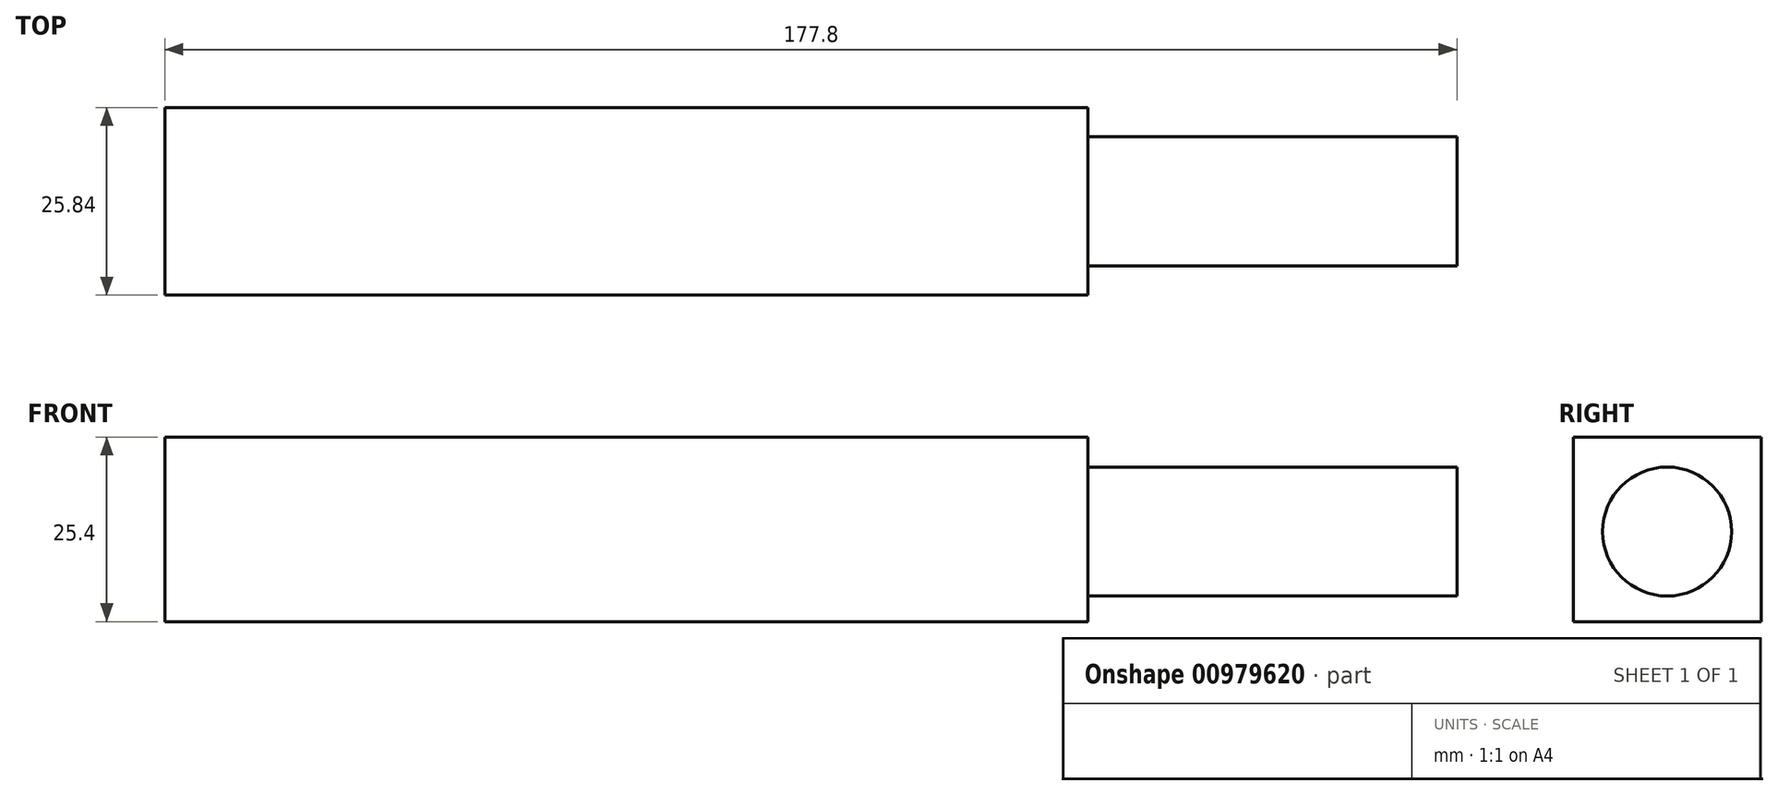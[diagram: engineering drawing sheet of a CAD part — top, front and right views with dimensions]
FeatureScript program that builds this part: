
annotation { "Feature Type Name" : "Feature", "Feature Type Description" : "" }
export const myFeature = defineFeature(function(context is Context, id is Id, definition is map)
    precondition{}
    {
        {
            var Q0;
            Q0=qCreatedBy(makeId("Top.planeOp"),FACE);
            var sketch = newSketch(context, id + "F0", { "sketchPlane" : qUnion([Q0])});
            skLineSegment(sketch, "E0.bottom", {"start": v(-50.8, -12.92) * mm, "end": v(50.8, -12.92) * mm});
            skLineSegment(sketch, "E0.top", {"start": v(-50.8, 12.92) * mm, "end": v(50.8, 12.92) * mm});
            skLineSegment(sketch, "E0.left", {"start": v(-50.8, -12.92) * mm, "end": v(-50.8, 12.92) * mm});
            skLineSegment(sketch, "E0.right", {"start": v(50.8, -12.92) * mm, "end": v(50.8, 12.92) * mm});
            skPoint(sketch, "E0.middle", {"position": v(0, 0) * mm});
            skSolve(sketch);
        }
        {
            var Q0;
            Q0=makeQuery(id+"F0.imprint","IMPRINT",FACE,{"disambiguationData":[TD([[makeQuery(id+"F0.imprint","IMPRINT",EDGE,{"derivedFrom":sQuery(id+"F0.wireOp",EDGE,"E0.bottom")}),1.0]])]});
            extrude(context, id + "F1", {"entities" : qUnion([Q0]), "depth" : 25.4 * mm, "offsetDistance" : 25.4 * mm});
        }
        {
            var Q0;
            Q0=makeQuery(id+"F1.opExtrude","SWEPT_FACE",FACE,{"disambiguationData":[OSD([sQuery(id+"F0.wireOp",EDGE,"E0.right")])]});
            var sketch = newSketch(context, id + "F2", { "sketchPlane" : qUnion([Q0])});
            skCircle(sketch, "E1", {"center": v(0, 12.38) * mm, "radius": 8.88 * mm});
            skSolve(sketch);
        }
        {
            var Q0;
            Q0=makeQuery(id+"F1.opExtrude","SWEPT_FACE",FACE,{"disambiguationData":[OSD([sQuery(id+"F0.wireOp",EDGE,"E0.left")])]});
            extrude(context, id + "F3", {"entities" : qUnion([Q0]), "operationType" : NewBodyOperationType.ADD, "depth" : 25.4 * mm, "offsetDistance" : 25.4 * mm});
        }
        {
            var Q0;
            Q0=makeQuery(id+"F2.imprint","IMPRINT",FACE,{"disambiguationData":[TD([[makeQuery(id+"F2.imprint","IMPRINT",EDGE,{"derivedFrom":sQuery(id+"F2.wireOp",EDGE,"E1")}),1.0]])]});
            extrude(context, id + "F4", {"entities" : qUnion([Q0]), "operationType" : NewBodyOperationType.ADD, "depth" : 25.4 * mm, "offsetDistance" : 25.4 * mm});
        }
        {
            var Q0;
            Q0=makeQuery(id+"F4.opExtrude","CAP_FACE",FACE,{"disambiguationData":[OSD([sQuery(id+"F2.wireOp",EDGE,"E1")])],"isStart":false});
            extrude(context, id + "F5", {"entities" : qUnion([Q0]), "operationType" : NewBodyOperationType.ADD, "depth" : 25.4 * mm, "offsetDistance" : 25.4 * mm});
        }
    });
